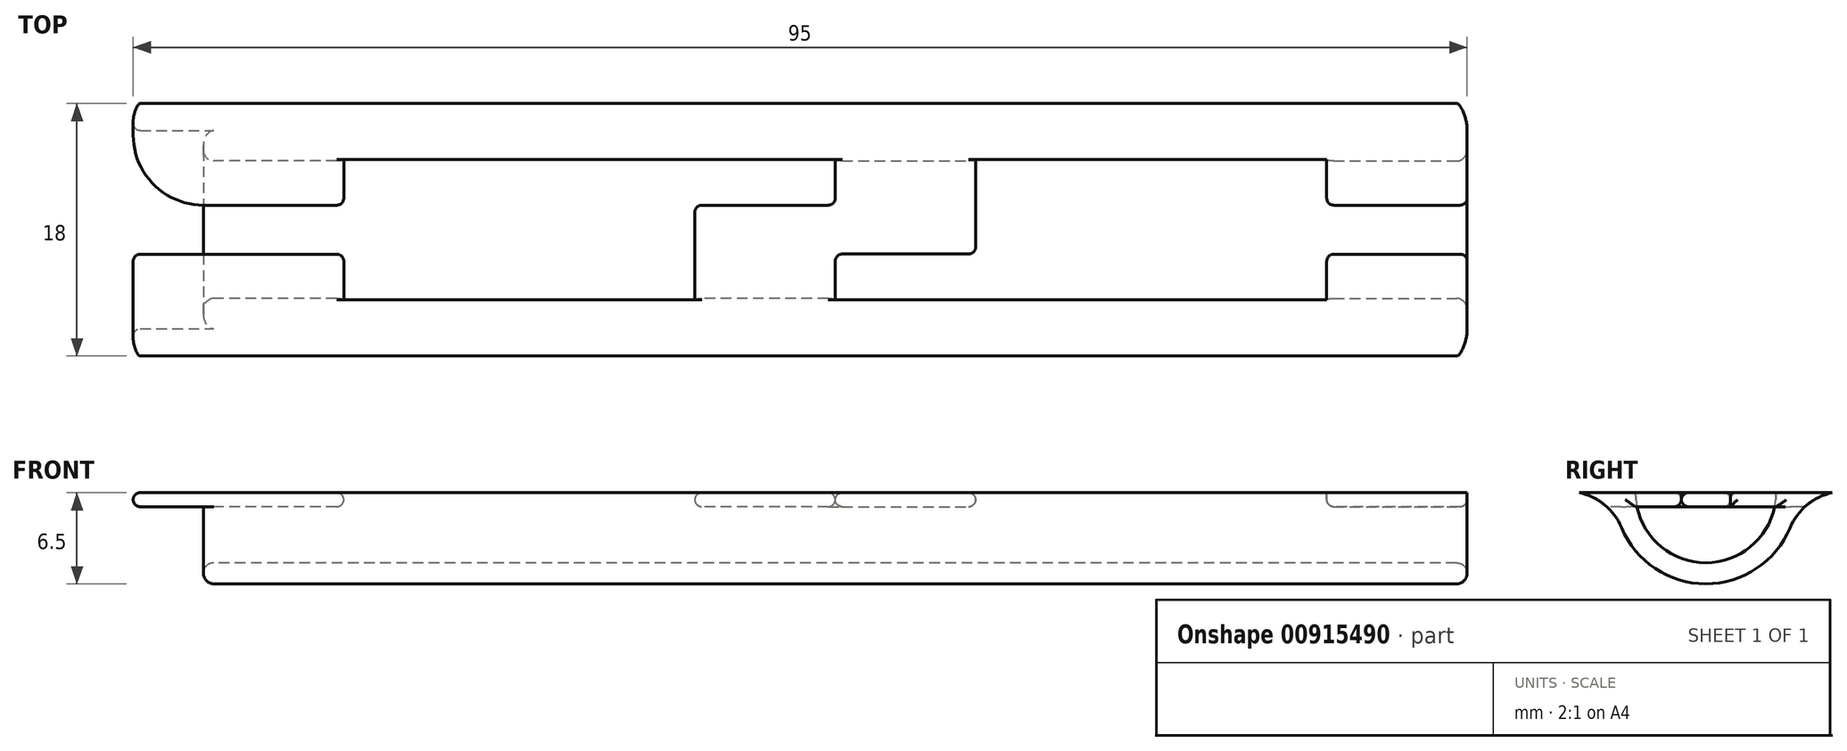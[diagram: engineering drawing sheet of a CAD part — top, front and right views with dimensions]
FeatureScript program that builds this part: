
annotation { "Feature Type Name" : "Feature", "Feature Type Description" : "" }
export const myFeature = defineFeature(function(context is Context, id is Id, definition is map)
    precondition{}
    {
        {
            var Q0;
            Q0=qCreatedBy(makeId("Right.planeOp"),FACE);
            var sketch = newSketch(context, id + "F0", { "sketchPlane" : qUnion([Q0])});
            skArc(sketch, "E0", {"start": v(-5, 0) * mm, "mid": v(0, -5) * mm, "end": v(5, 0) * mm});
            skArc(sketch, "E1", {"start": v(-6, -2.5) * mm, "mid": v(0, -6.5) * mm, "end": v(6, -2.5) * mm});
            skArc(sketch, "E2", {"start": v(6, -2.5) * mm, "mid": v(7.2, -0.88) * mm, "end": v(9, 0) * mm});
            skArc(sketch, "E3", {"start": v(-6, -2.5) * mm, "mid": v(-7.2, -0.88) * mm, "end": v(-9, 0) * mm});
            skLineSegment(sketch, "E4", {"start": v(9, 0) * mm, "end": v(5, 0) * mm});
            skLineSegment(sketch, "E5", {"start": v(-5, 0) * mm, "end": v(-9, 0) * mm});
            skLineSegment(sketch, "E6", {"start": v(-5, 0) * mm, "end": v(5, 0) * mm});
            skLineSegment(sketch, "E7", {"start": v(-4.9, -1) * mm, "end": v(4.9, -1) * mm});
            skLineSegment(sketch, "E8", {"start": v(-7.06, -1) * mm, "end": v(-4.9, -1) * mm});
            skLineSegment(sketch, "E9", {"start": v(4.9, -1) * mm, "end": v(7.06, -1) * mm});
            skLineSegment(sketch, "E10", {"start": v(1.75, -1) * mm, "end": v(1.75, 0) * mm});
            skLineSegment(sketch, "E11", {"start": v(-1.75, -1) * mm, "end": v(-1.75, 0) * mm});
            skSolve(sketch);
        }
        {
            var Q0;
            Q0=makeQuery(id+"F0.imprint","IMPRINT",FACE,{"disambiguationData":[TD([[makeQuery(id+"F0.imprint","IMPRINT",EDGE,{"derivedFrom":sQuery(id+"F0.wireOp",EDGE,"E1")}),1.0]])]});
            var Q1;
            {var subQ0=sQuery(id+"F0.wireOp",EDGE,"E5");Q1=makeQuery(id+"F0.imprint","IMPRINT",FACE,{"disambiguationData":[TD([[makeQuery(id+"F0.imprint","IMPRINT",EDGE,{"derivedFrom":subQ0}),1.0]])]});}
            var Q2;
            {var subQ0=sQuery(id+"F0.wireOp",EDGE,"E4");Q2=makeQuery(id+"F0.imprint","IMPRINT",FACE,{"disambiguationData":[TD([[makeQuery(id+"F0.imprint","IMPRINT",EDGE,{"derivedFrom":subQ0}),1.0]])]});}
            extrude(context, id + "F1", {"entities" : qUnion([Q0, Q1, Q2]), "depth" : 90 * mm, "offsetDistance" : 25 * mm});
        }
        {
            var Q0;
            {var subQ0=sQuery(id+"F0.wireOp",EDGE,"E6");Q0=makeQuery(id+"F0.imprint","IMPRINT",FACE,{"disambiguationData":[TD([[makeQuery(id+"F0.imprint","IMPRINT",EDGE,{"derivedFrom":subQ0}),-1.0]])]});}
            extrude(context, id + "F2", {"entities" : qUnion([Q0]), "operationType" : NewBodyOperationType.ADD, "depth" : 10 * mm, "offsetDistance" : 25 * mm});
        }
        {
            var Q0;
            {var subQ0=sQuery(id+"F0.wireOp",EDGE,"E4");Q0=makeQuery(id+"F0.imprint","IMPRINT",FACE,{"disambiguationData":[TD([[makeQuery(id+"F0.imprint","IMPRINT",EDGE,{"derivedFrom":subQ0}),1.0]])]});}
            var Q1;
            {var subQ0=sQuery(id+"F0.wireOp",EDGE,"E6");Q1=makeQuery(id+"F0.imprint","IMPRINT",FACE,{"disambiguationData":[TD([[makeQuery(id+"F0.imprint","IMPRINT",EDGE,{"derivedFrom":subQ0}),-1.0]])]});}
            var Q2;
            {var subQ0=sQuery(id+"F0.wireOp",EDGE,"E5");Q2=makeQuery(id+"F0.imprint","IMPRINT",FACE,{"disambiguationData":[TD([[makeQuery(id+"F0.imprint","IMPRINT",EDGE,{"derivedFrom":subQ0}),1.0]])]});}
            extrude(context, id + "F3", {"entities" : qUnion([Q0, Q1, Q2]), "operationType" : NewBodyOperationType.ADD, "oppositeDirection" : true, "depth" : 5 * mm, "offsetDistance" : 25 * mm});
        }
        {
            var Q0;
            Q0=makeQuery(id+"F1.opExtrude","CAP_FACE",FACE,{"disambiguationData":[OSD([sQuery(id+"F0.wireOp",EDGE,"E0"),sQuery(id+"F0.wireOp",EDGE,"E1"),sQuery(id+"F0.wireOp",EDGE,"E2"),sQuery(id+"F0.wireOp",EDGE,"E3"),sQuery(id+"F0.wireOp",EDGE,"E4"),sQuery(id+"F0.wireOp",EDGE,"E5")])],"isStart":false});
            var sketch = newSketch(context, id + "F4", { "sketchPlane" : qUnion([Q0])});
            skLineSegment(sketch, "E12", {"start": v(5, 0) * mm, "end": v(-5, 0) * mm});
            skLineSegment(sketch, "E13", {"start": v(4.9, -1) * mm, "end": v(-4.9, -1) * mm});
            skLineSegment(sketch, "E14", {"start": v(1.76, -1) * mm, "end": v(1.76, 0) * mm});
            skLineSegment(sketch, "E15", {"start": v(-1.74, -1) * mm, "end": v(-1.74, 0) * mm});
            skSolve(sketch);
        }
        {
            var Q0;
            {var subQ0=sQuery(id+"F4.wireOp",EDGE,"E12");Q0=makeQuery(id+"F4.imprint","IMPRINT",FACE,{"disambiguationData":[TD([[makeQuery(id+"F4.imprint","IMPRINT",EDGE,{"derivedFrom":subQ0}),1.0]])]});}
            extrude(context, id + "F5", {"entities" : qUnion([Q0]), "operationType" : NewBodyOperationType.ADD, "oppositeDirection" : true, "depth" : 10 * mm, "offsetDistance" : 25 * mm});
        }
        {
            var Q0;
            Q0=makeQuery(id+"F1.opExtrude","CAP_EDGE",EDGE,{"disambiguationData":[OSD([sQuery(id+"F0.wireOp",EDGE,"E1")])],"isStart":true});
            var Q1;
            Q1=makeQuery(id+"F1.opExtrude","CAP_EDGE",EDGE,{"disambiguationData":[OSD([sQuery(id+"F0.wireOp",EDGE,"E0")])],"isStart":true});
            var Q2;
            Q2=makeQuery(id+"F1.opExtrude","CAP_EDGE",EDGE,{"disambiguationData":[OSD([sQuery(id+"F0.wireOp",EDGE,"E3")])],"isStart":true});
            var Q3;
            Q3=makeQuery(id+"F1.opExtrude","CAP_EDGE",EDGE,{"disambiguationData":[OSD([sQuery(id+"F0.wireOp",EDGE,"E1")])],"isStart":false});
            var Q4;
            Q4=makeQuery(id+"F1.opExtrude","CAP_EDGE",EDGE,{"disambiguationData":[OSD([sQuery(id+"F0.wireOp",EDGE,"E0")])],"isStart":false});
            var Q5;
            Q5=makeQuery(id+"F1.opExtrude","CAP_EDGE",EDGE,{"disambiguationData":[OSD([sQuery(id+"F0.wireOp",EDGE,"E2")])],"isStart":false});
            fillet(context, id + "F6", {"entities" : qUnion([Q0, Q1, Q2, Q3, Q4, Q5]), "radius" : 0.75 * mm, "tangentPropagation" : true, "allowEdgeOverflow" : false});
        }
        {
            var Q0;
            {var subQ0=sQuery(id+"F0.wireOp",EDGE,"E10");Q0=makeQuery(id+"F0.imprint","IMPRINT",FACE,{"disambiguationData":[TD([[makeQuery(id+"F0.imprint","IMPRINT",EDGE,{"derivedFrom":subQ0}),1.0]])]});}
            extrude(context, id + "F7", {"entities" : qUnion([Q0]), "operationType" : NewBodyOperationType.REMOVE, "endBound" : BoundingType.THROUGH_ALL, "depth" : 25 * mm, "offsetDistance" : 25 * mm, "hasSecondDirection" : true, "secondDirectionOppositeDirection" : true, "secondDirectionDepth" : 25 * mm});
        }
        {
            var Q0;
            {var subQ1=sQuery(id+"F0.wireOp",EDGE,"E7");Q0=makeQuery(id+"F7.boolean.opBoolean","COPY",FACE,{"disambiguationData":[TD([makeQuery(id+"F2.opExtrude","SWEPT_FACE",FACE,{"disambiguationData":[OSD([subQ1])]})])],"derivedFrom":makeQuery(id+"F7.opExtrude","SWEPT_FACE",FACE,{"disambiguationData":[OSD([sQuery(id+"F0.wireOp",EDGE,"E11")])]})});}
            var Q1;
            {var subQ0=sQuery(id+"F0.wireOp",EDGE,"E7");Q1=makeQuery(id+"F7.boolean.opBoolean","SPLIT",EDGE,{"disambiguationData":[TD([makeQuery(id+"F7.opExtrude","SWEPT_FACE",FACE,{"disambiguationData":[OSD([sQuery(id+"F0.wireOp",EDGE,"E11")])]})])],"derivedFrom":makeQuery(id+"F2.opExtrude","CAP_EDGE",EDGE,{"disambiguationData":[OSD([subQ0])],"isStart":false})});}
            var Q2;
            {var subQ0=sQuery(id+"F0.wireOp",EDGE,"E6");Q2=makeQuery(id+"F7.boolean.opBoolean","SPLIT",EDGE,{"disambiguationData":[TD([makeQuery(id+"F7.opExtrude","SWEPT_FACE",FACE,{"disambiguationData":[OSD([sQuery(id+"F0.wireOp",EDGE,"E11")])]})])],"derivedFrom":makeQuery(id+"F2.opExtrude","CAP_EDGE",EDGE,{"disambiguationData":[OSD([subQ0])],"isStart":false})});}
            var Q3;
            {var subQ0=sQuery(id+"F0.wireOp",EDGE,"E6");Q3=makeQuery(id+"F7.boolean.opBoolean","SPLIT",EDGE,{"disambiguationData":[TD([makeQuery(id+"F7.opExtrude","SWEPT_FACE",FACE,{"disambiguationData":[OSD([sQuery(id+"F0.wireOp",EDGE,"E10")])]})])],"derivedFrom":makeQuery(id+"F2.opExtrude","CAP_EDGE",EDGE,{"disambiguationData":[OSD([subQ0])],"isStart":false})});}
            var Q4;
            {var subQ0=sQuery(id+"F0.wireOp",EDGE,"E7");Q4=makeQuery(id+"F7.boolean.opBoolean","SPLIT",EDGE,{"disambiguationData":[TD([makeQuery(id+"F7.opExtrude","SWEPT_FACE",FACE,{"disambiguationData":[OSD([sQuery(id+"F0.wireOp",EDGE,"E10")])]})])],"derivedFrom":makeQuery(id+"F2.opExtrude","CAP_EDGE",EDGE,{"disambiguationData":[OSD([subQ0])],"isStart":false})});}
            var Q5;
            {var subQ0=sQuery(id+"F0.wireOp",EDGE,"E3");var subQ1=sQuery(id+"F0.wireOp",EDGE,"E7");var subQ2=sQuery(id+"F0.wireOp",EDGE,"E9");var subQ3=sQuery(id+"F0.wireOp",EDGE,"E8");Q5=makeQuery(id+"F7.boolean.opBoolean","SPLIT",EDGE,{"disambiguationData":[TD([makeQuery(id+"F1.opExtrude","SWEPT_FACE",FACE,{"disambiguationData":[OSD([subQ0])]})])],"derivedFrom":makeQuery(id+"F3.opExtrude","CAP_EDGE",EDGE,{"disambiguationData":[OSD([subQ1,subQ3,subQ2])],"isStart":false})});}
            var Q6;
            {var subQ0=sQuery(id+"F0.wireOp",EDGE,"E5");var subQ1=sQuery(id+"F0.wireOp",EDGE,"E4");var subQ2=sQuery(id+"F0.wireOp",EDGE,"E6");var subQ3=sQuery(id+"F0.wireOp",EDGE,"E3");Q6=makeQuery(id+"F7.boolean.opBoolean","SPLIT",EDGE,{"disambiguationData":[TD([makeQuery(id+"F1.opExtrude","SWEPT_FACE",FACE,{"disambiguationData":[OSD([subQ3])]})])],"derivedFrom":makeQuery(id+"F3.opExtrude","CAP_EDGE",EDGE,{"disambiguationData":[OSD([subQ1,subQ0,subQ2])],"isStart":false})});}
            fillet(context, id + "F8", {"entities" : qUnion([Q0, Q1, Q2, Q3, Q4, Q5, Q6]), "radius" : 0.5 * mm, "tangentPropagation" : true, "allowEdgeOverflow" : false});
        }
        {
            var Q0;
            {var subQ5=sQuery(id+"F0.wireOp",EDGE,"E11");Q0=makeQuery(id+"F0.imprint","IMPRINT",FACE,{"disambiguationData":[TD([[makeQuery(id+"F0.imprint","IMPRINT",EDGE,{"derivedFrom":subQ5}),1.0]])]});}
            var Q1;
            {var subQ0=sQuery(id+"F0.wireOp",EDGE,"E10");Q1=makeQuery(id+"F0.imprint","IMPRINT",FACE,{"disambiguationData":[TD([[makeQuery(id+"F0.imprint","IMPRINT",EDGE,{"derivedFrom":subQ0}),1.0]])]});}
            extrude(context, id + "F9", {"entities" : qUnion([Q0, Q1]), "operationType" : NewBodyOperationType.ADD, "depth" : 45 * mm, "offsetDistance" : 25 * mm, "hasSecondDirection" : true, "secondDirectionOppositeDirection" : true, "secondDirectionDepth" : -35 * mm});
        }
        {
            var Q0;
            {var subQ0=sQuery(id+"F4.wireOp",EDGE,"E14");Q0=makeQuery(id+"F4.imprint","IMPRINT",FACE,{"disambiguationData":[TD([[makeQuery(id+"F4.imprint","IMPRINT",EDGE,{"derivedFrom":subQ0}),1.0]])]});}
            var Q1;
            {var subQ3=sQuery(id+"F4.wireOp",EDGE,"E14");Q1=makeQuery(id+"F4.imprint","IMPRINT",FACE,{"disambiguationData":[TD([[makeQuery(id+"F4.imprint","IMPRINT",EDGE,{"derivedFrom":subQ3}),-1.0]])]});}
            extrude(context, id + "F10", {"entities" : qUnion([Q0, Q1]), "operationType" : NewBodyOperationType.ADD, "oppositeDirection" : true, "depth" : 45 * mm, "offsetDistance" : 25 * mm, "hasSecondDirection" : true, "secondDirectionOppositeDirection" : false, "secondDirectionDepth" : -35 * mm});
        }
        {
            var Q0;
            Q0=makeQuery(id+"F10.opExtrude","CAP_EDGE",EDGE,{"disambiguationData":[OSD([sQuery(id+"F4.wireOp",EDGE,"E13")])],"isStart":true});
            var Q1;
            Q1=makeQuery(id+"F10.opExtrude","CAP_EDGE",EDGE,{"disambiguationData":[OSD([sQuery(id+"F4.wireOp",EDGE,"E15")])],"isStart":true});
            var Q2;
            Q2=makeQuery(id+"F10.opExtrude","SWEPT_FACE",FACE,{"disambiguationData":[OSD([sQuery(id+"F4.wireOp",EDGE,"E15")])]});
            var Q3;
            Q3=makeQuery(id+"F10.opExtrude","CAP_EDGE",EDGE,{"disambiguationData":[OSD([sQuery(id+"F4.wireOp",EDGE,"E12")])],"isStart":true});
            var Q4;
            Q4=makeQuery(id+"F10.opExtrude","CAP_EDGE",EDGE,{"disambiguationData":[OSD([sQuery(id+"F4.wireOp",EDGE,"E12")])],"isStart":false});
            var Q5;
            Q5=makeQuery(id+"F10.opExtrude","CAP_EDGE",EDGE,{"disambiguationData":[OSD([sQuery(id+"F4.wireOp",EDGE,"E13")])],"isStart":false});
            var Q6;
            Q6=makeQuery(id+"F9.opExtrude","CAP_EDGE",EDGE,{"disambiguationData":[OSD([sQuery(id+"F0.wireOp",EDGE,"E6")])],"isStart":true});
            var Q7;
            Q7=makeQuery(id+"F9.opExtrude","CAP_EDGE",EDGE,{"disambiguationData":[OSD([sQuery(id+"F0.wireOp",EDGE,"E7")])],"isStart":true});
            var Q8;
            Q8=makeQuery(id+"F9.opExtrude","SWEPT_FACE",FACE,{"disambiguationData":[OSD([sQuery(id+"F0.wireOp",EDGE,"E10")])]});
            var Q9;
            Q9=makeQuery(id+"F9.opExtrude","CAP_EDGE",EDGE,{"disambiguationData":[OSD([sQuery(id+"F0.wireOp",EDGE,"E7")])],"isStart":false});
            var Q10;
            Q10=makeQuery(id+"F9.opExtrude","CAP_EDGE",EDGE,{"disambiguationData":[OSD([sQuery(id+"F0.wireOp",EDGE,"E6")])],"isStart":false});
            fillet(context, id + "F11", {"entities" : qUnion([Q0, Q1, Q2, Q3, Q4, Q5, Q6, Q7, Q8, Q9, Q10]), "radius" : 0.5 * mm, "tangentPropagation" : true, "allowEdgeOverflow" : false});
        }
        {
            var Q0;
            Q0=makeQuery(id+"F7.boolean.opBoolean","INTERSECT",EDGE,{"derivedFrom":[makeQuery(id+"F3.opExtrude","CAP_FACE",FACE,{"disambiguationData":[OSD([sQuery(id+"F0.wireOp",EDGE,"E2"),sQuery(id+"F0.wireOp",EDGE,"E3"),sQuery(id+"F0.wireOp",EDGE,"E4"),sQuery(id+"F0.wireOp",EDGE,"E5"),sQuery(id+"F0.wireOp",EDGE,"E6"),sQuery(id+"F0.wireOp",EDGE,"E7"),sQuery(id+"F0.wireOp",EDGE,"E8"),sQuery(id+"F0.wireOp",EDGE,"E9")])],"isStart":false}),makeQuery(id+"F7.opExtrude","SWEPT_FACE",FACE,{"disambiguationData":[OSD([sQuery(id+"F0.wireOp",EDGE,"E10")])]})]});
            fillet(context, id + "F12", {"entities" : qUnion([Q0]), "radius" : 5 * mm, "tangentPropagation" : true, "allowEdgeOverflow" : false});
        }
        {
            var Q0;
            {var subQ0=sQuery(id+"F0.wireOp",EDGE,"E7");var subQ1=sQuery(id+"F0.wireOp",EDGE,"E10");Q0=makeQuery(id+"F7.boolean.opBoolean","COPY",EDGE,{"disambiguationData":[topologyDisambiguationEdgeConnected([makeQuery(id+"F2.opExtrude","SWEPT_FACE",FACE,{"disambiguationData":[OSD([subQ0])]})])],"derivedFrom":makeQuery(id+"F7.opExtrude","SWEPT_EDGE",EDGE,{"disambiguationData":[OSD([subQ0,subQ1])]})});}
            var Q1;
            {var subQ0=sQuery(id+"F0.wireOp",EDGE,"E6");var subQ1=sQuery(id+"F0.wireOp",EDGE,"E7");var subQ4=sQuery(id+"F0.wireOp",EDGE,"E10");Q1=makeQuery(id+"F7.boolean.opBoolean","COPY",EDGE,{"disambiguationData":[TD([makeQuery(id+"F2.opExtrude","CAP_FACE",FACE,{"disambiguationData":[OSD([sQuery(id+"F0.wireOp",EDGE,"E0"),subQ0,subQ1])],"isStart":false})])],"derivedFrom":makeQuery(id+"F7.opExtrude","SWEPT_EDGE",EDGE,{"disambiguationData":[OSD([subQ0,subQ4])]})});}
            fillet(context, id + "F13", {"entities" : qUnion([Q0, Q1]), "radius" : 0.5 * mm, "tangentPropagation" : true, "allowEdgeOverflow" : false});
        }
        {
            var Q0;
            {var subQ1=sQuery(id+"F4.wireOp",EDGE,"E13");Q0=makeQuery(id+"F7.boolean.opBoolean","SPLIT",EDGE,{"disambiguationData":[TD([makeQuery(id+"F7.opExtrude","SWEPT_FACE",FACE,{"disambiguationData":[OSD([sQuery(id+"F0.wireOp",EDGE,"E11")])]})])],"derivedFrom":makeQuery(id+"F5.opExtrude","CAP_EDGE",EDGE,{"disambiguationData":[OSD([subQ1])],"isStart":false})});}
            var Q1;
            {var subQ0=sQuery(id+"F0.wireOp",EDGE,"E11");Q1=makeQuery(id+"F7.boolean.opBoolean","COPY",EDGE,{"disambiguationData":[topologyDisambiguationEdgeConnected([makeQuery(id+"F5.opExtrude","SWEPT_FACE",FACE,{"disambiguationData":[OSD([sQuery(id+"F4.wireOp",EDGE,"E13")])]})])],"derivedFrom":makeQuery(id+"F7.opExtrude","SWEPT_EDGE",EDGE,{"disambiguationData":[OSD([sQuery(id+"F0.wireOp",EDGE,"E7"),subQ0])]})});}
            var Q2;
            Q2=makeQuery(id+"F7.boolean.opBoolean","INTERSECT",EDGE,{"derivedFrom":[makeQuery(id+"F5.opExtrude","CAP_FACE",FACE,{"disambiguationData":[OSD([sQuery(id+"F0.wireOp",EDGE,"E0"),sQuery(id+"F4.wireOp",EDGE,"E12"),sQuery(id+"F4.wireOp",EDGE,"E13")])],"isStart":false}),makeQuery(id+"F7.opExtrude","SWEPT_FACE",FACE,{"disambiguationData":[OSD([sQuery(id+"F0.wireOp",EDGE,"E11")])]})]});
            var Q3;
            {var subQ0=sQuery(id+"F0.wireOp",EDGE,"E0");Q3=makeQuery(id+"F7.boolean.opBoolean","INTERSECT",EDGE,{"derivedFrom":[makeQuery(id+"F5.boolean.opBoolean","MERGE",FACE,{"derivedFrom":[makeQuery(id+"F1.opExtrude","CAP_FACE",FACE,{"disambiguationData":[OSD([subQ0,sQuery(id+"F0.wireOp",EDGE,"E1"),sQuery(id+"F0.wireOp",EDGE,"E2"),sQuery(id+"F0.wireOp",EDGE,"E3"),sQuery(id+"F0.wireOp",EDGE,"E4"),sQuery(id+"F0.wireOp",EDGE,"E5")])],"isStart":false}),makeQuery(id+"F5.opExtrude","CAP_FACE",FACE,{"disambiguationData":[OSD([subQ0,sQuery(id+"F4.wireOp",EDGE,"E12"),sQuery(id+"F4.wireOp",EDGE,"E13")])],"isStart":true})]}),makeQuery(id+"F7.opExtrude","SWEPT_FACE",FACE,{"disambiguationData":[OSD([sQuery(id+"F0.wireOp",EDGE,"E11")])]})]});}
            var Q4;
            {var subQ1=sQuery(id+"F4.wireOp",EDGE,"E13");Q4=makeQuery(id+"F7.boolean.opBoolean","SPLIT",EDGE,{"disambiguationData":[TD([makeQuery(id+"F7.opExtrude","SWEPT_FACE",FACE,{"disambiguationData":[OSD([sQuery(id+"F0.wireOp",EDGE,"E11")])]})])],"derivedFrom":makeQuery(id+"F5.opExtrude","CAP_EDGE",EDGE,{"disambiguationData":[OSD([subQ1])],"isStart":true})});}
            var Q5;
            Q5=makeQuery(id+"F7.boolean.opBoolean","INTERSECT",EDGE,{"derivedFrom":[makeQuery(id+"F5.opExtrude","CAP_FACE",FACE,{"disambiguationData":[OSD([sQuery(id+"F0.wireOp",EDGE,"E0"),sQuery(id+"F4.wireOp",EDGE,"E12"),sQuery(id+"F4.wireOp",EDGE,"E13")])],"isStart":false}),makeQuery(id+"F7.opExtrude","SWEPT_FACE",FACE,{"disambiguationData":[OSD([sQuery(id+"F0.wireOp",EDGE,"E10")])]})]});
            var Q6;
            {var subQ1=sQuery(id+"F4.wireOp",EDGE,"E13");Q6=makeQuery(id+"F7.boolean.opBoolean","SPLIT",EDGE,{"disambiguationData":[TD([makeQuery(id+"F7.opExtrude","SWEPT_FACE",FACE,{"disambiguationData":[OSD([sQuery(id+"F0.wireOp",EDGE,"E10")])]})])],"derivedFrom":makeQuery(id+"F5.opExtrude","CAP_EDGE",EDGE,{"disambiguationData":[OSD([subQ1])],"isStart":false})});}
            var Q7;
            {var subQ0=sQuery(id+"F0.wireOp",EDGE,"E10");Q7=makeQuery(id+"F7.boolean.opBoolean","COPY",EDGE,{"disambiguationData":[topologyDisambiguationEdgeConnected([makeQuery(id+"F5.opExtrude","SWEPT_FACE",FACE,{"disambiguationData":[OSD([sQuery(id+"F4.wireOp",EDGE,"E13")])]})])],"derivedFrom":makeQuery(id+"F7.opExtrude","SWEPT_EDGE",EDGE,{"disambiguationData":[OSD([sQuery(id+"F0.wireOp",EDGE,"E7"),subQ0])]})});}
            var Q8;
            {var subQ1=sQuery(id+"F4.wireOp",EDGE,"E13");Q8=makeQuery(id+"F7.boolean.opBoolean","SPLIT",EDGE,{"disambiguationData":[TD([makeQuery(id+"F7.opExtrude","SWEPT_FACE",FACE,{"disambiguationData":[OSD([sQuery(id+"F0.wireOp",EDGE,"E10")])]})])],"derivedFrom":makeQuery(id+"F5.opExtrude","CAP_EDGE",EDGE,{"disambiguationData":[OSD([subQ1])],"isStart":true})});}
            var Q9;
            {var subQ0=sQuery(id+"F0.wireOp",EDGE,"E0");Q9=makeQuery(id+"F7.boolean.opBoolean","INTERSECT",EDGE,{"derivedFrom":[makeQuery(id+"F5.boolean.opBoolean","MERGE",FACE,{"derivedFrom":[makeQuery(id+"F1.opExtrude","CAP_FACE",FACE,{"disambiguationData":[OSD([subQ0,sQuery(id+"F0.wireOp",EDGE,"E1"),sQuery(id+"F0.wireOp",EDGE,"E2"),sQuery(id+"F0.wireOp",EDGE,"E3"),sQuery(id+"F0.wireOp",EDGE,"E4"),sQuery(id+"F0.wireOp",EDGE,"E5")])],"isStart":false}),makeQuery(id+"F5.opExtrude","CAP_FACE",FACE,{"disambiguationData":[OSD([subQ0,sQuery(id+"F4.wireOp",EDGE,"E12"),sQuery(id+"F4.wireOp",EDGE,"E13")])],"isStart":true})]}),makeQuery(id+"F7.opExtrude","SWEPT_FACE",FACE,{"disambiguationData":[OSD([sQuery(id+"F0.wireOp",EDGE,"E10")])]})]});}
            fillet(context, id + "F14", {"entities" : qUnion([Q0, Q1, Q2, Q3, Q4, Q5, Q6, Q7, Q8, Q9]), "radius" : 0.5 * mm, "tangentPropagation" : true, "allowEdgeOverflow" : false});
        }
    });
